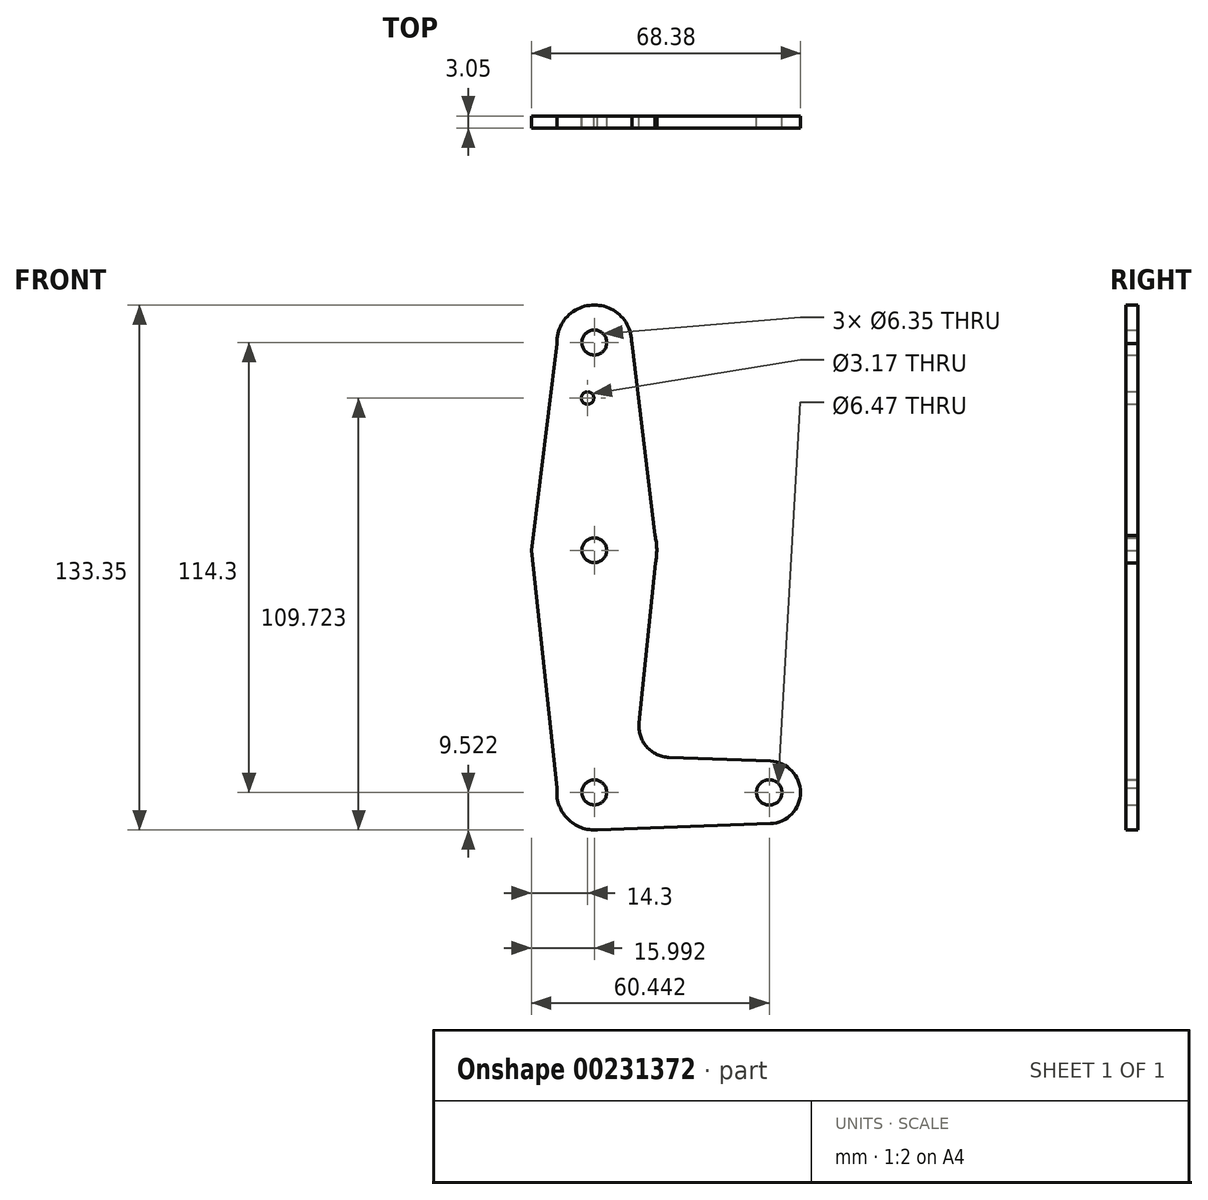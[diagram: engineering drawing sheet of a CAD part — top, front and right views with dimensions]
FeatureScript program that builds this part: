
annotation { "Feature Type Name" : "Feature", "Feature Type Description" : "" }
export const myFeature = defineFeature(function(context is Context, id is Id, definition is map)
    precondition{}
    {
        {
            var Q0;
            Q0=qCreatedBy(makeId("Front.planeOp"),FACE);
            var sketch = newSketch(context, id + "F0", { "sketchPlane" : qUnion([Q0])});
            skLineSegment(sketch, "E0", {"start": v(-38.07, 52.78) * mm, "end": v(-38.07, -61.52) * mm, "construction": true});
            skLineSegment(sketch, "E1", {"start": v(-38.07, -61.52) * mm, "end": v(6.38, -61.52) * mm, "construction": true});
            skCircle(sketch, "E2", {"center": v(-38.07, 52.78) * mm, "radius": 9.53 * mm});
            skCircle(sketch, "E3", {"center": v(-38.07, 0) * mm, "radius": 15.88 * mm});
            skCircle(sketch, "E4", {"center": v(-38.07, -61.52) * mm, "radius": 9.53 * mm});
            skCircle(sketch, "E5", {"center": v(6.38, -61.52) * mm, "radius": 7.94 * mm});
            skLineSegment(sketch, "E6", {"start": v(-47.6, 52.55) * mm, "end": v(-54.06, 0) * mm});
            skLineSegment(sketch, "E7", {"start": v(-54.06, 0) * mm, "end": v(-47.52, -60.36) * mm});
            skLineSegment(sketch, "E8", {"start": v(-19.07, -52.62) * mm, "end": v(6.68, -53.59) * mm});
            skLineSegment(sketch, "E9", {"start": v(-38.26, -71.04) * mm, "end": v(6.66, -69.45) * mm});
            skLineSegment(sketch, "E10", {"start": v(-22.2, 0) * mm, "end": v(-26.69, -43.87) * mm});
            skLineSegment(sketch, "E11", {"start": v(-28.55, 52.54) * mm, "end": v(-22.2, 0) * mm});
            skCircle(sketch, "E12", {"center": v(-38.07, 52.78) * mm, "radius": 3.18 * mm});
            skCircle(sketch, "E13", {"center": v(-38.07, 0) * mm, "radius": 3.18 * mm});
            skCircle(sketch, "E14", {"center": v(-38.07, -61.52) * mm, "radius": 3.18 * mm});
            skCircle(sketch, "E15", {"center": v(6.38, -61.52) * mm, "radius": 3.24 * mm});
            skArc(sketch, "E16.filletArc", {"start": v(-26.69, -43.87) * mm, "mid": v(-24.78, -49.9) * mm, "end": v(-19.07, -52.62) * mm});
            skCircle(sketch, "E17", {"center": v(-39.76, 38.68) * mm, "radius": 1.59 * mm});
            skSolve(sketch);
        }
        {
            var Q0;
            Q0 = qSketchRegion(id + "F0", true);
            extrude(context, id + "F1", {"entities" : qUnion([Q0]), "depth" : 3.05 * mm});
        }
    });
